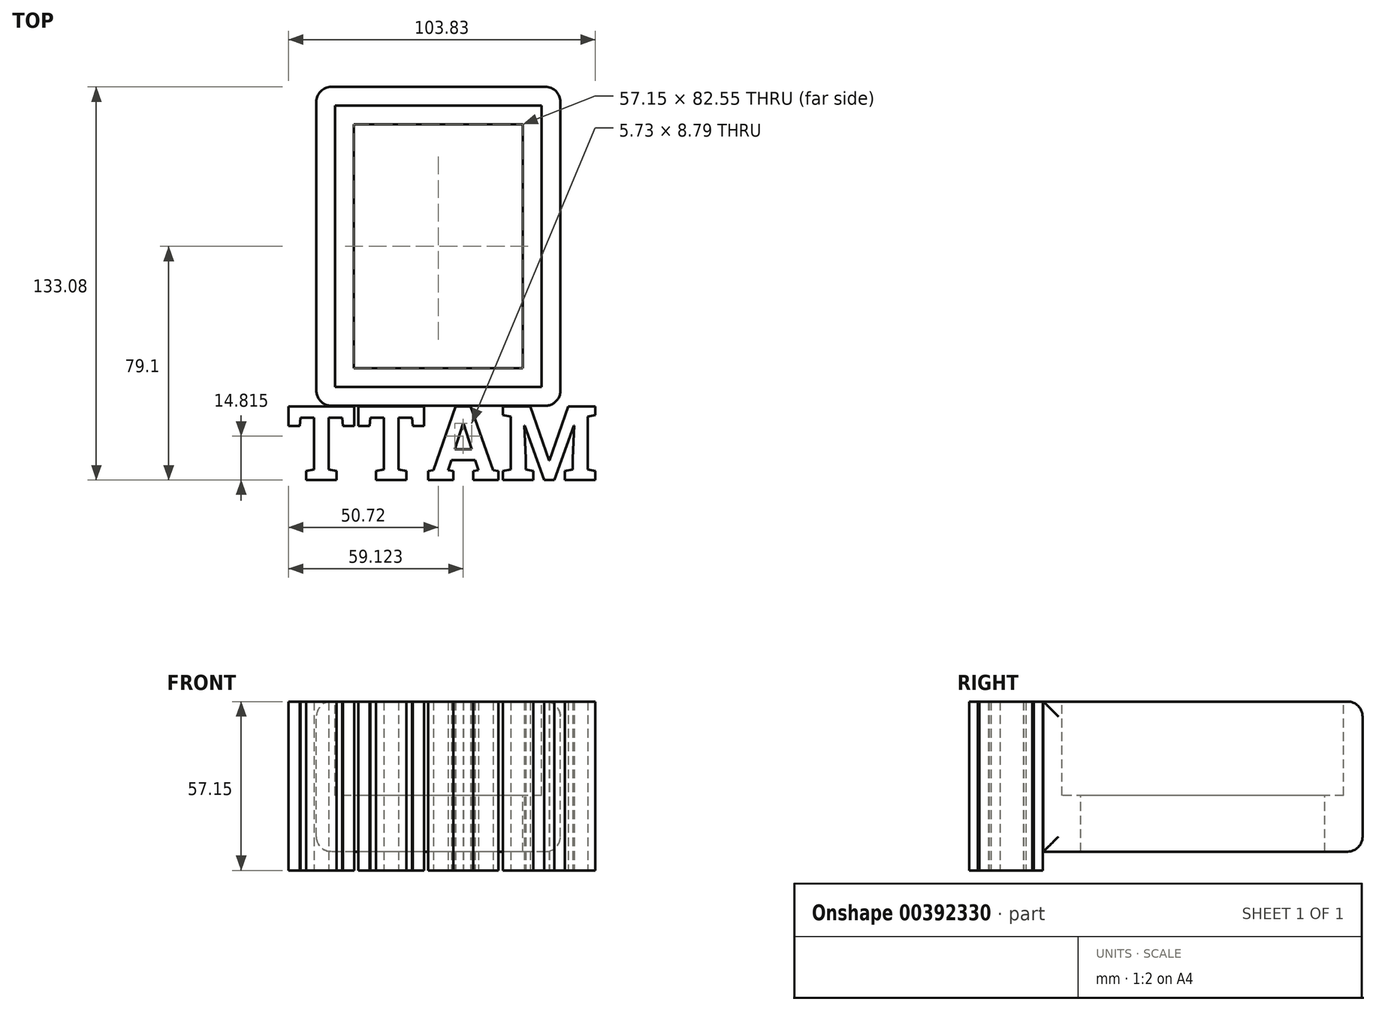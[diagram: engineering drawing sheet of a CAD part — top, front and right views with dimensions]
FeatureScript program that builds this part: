
annotation { "Feature Type Name" : "Feature", "Feature Type Description" : "" }
export const myFeature = defineFeature(function(context is Context, id is Id, definition is map)
    precondition{}
    {
        {
            var Q0;
            Q0=qCreatedBy(makeId("Top.planeOp"),FACE);
            var sketch = newSketch(context, id + "F0", { "sketchPlane" : qUnion([Q0])});
            skLineSegment(sketch, "E0.bottom", {"start": v(41.27, 53.98) * mm, "end": v(-41.28, 53.97) * mm});
            skLineSegment(sketch, "E0.top", {"start": v(41.28, -53.97) * mm, "end": v(-41.27, -53.98) * mm});
            skLineSegment(sketch, "E0.left", {"start": v(41.27, 53.98) * mm, "end": v(41.28, -53.97) * mm});
            skLineSegment(sketch, "E0.right", {"start": v(-41.28, 53.97) * mm, "end": v(-41.27, -53.98) * mm});
            skPoint(sketch, "E0.middle", {"position": v(0, 0) * mm});
            skSolve(sketch);
        }
        {
            var Q0;
            Q0=qCreatedBy(makeId("Top.planeOp"),FACE);
            var sketch = newSketch(context, id + "F1", { "sketchPlane" : qUnion([Q0])});
            skLineSegment(sketch, "E1.bottom", {"start": v(34.92, 47.63) * mm, "end": v(-34.93, 47.62) * mm});
            skLineSegment(sketch, "E1.top", {"start": v(34.93, -47.62) * mm, "end": v(-34.92, -47.63) * mm});
            skLineSegment(sketch, "E1.left", {"start": v(34.92, 47.63) * mm, "end": v(34.93, -47.62) * mm});
            skLineSegment(sketch, "E1.right", {"start": v(-34.93, 47.62) * mm, "end": v(-34.92, -47.63) * mm});
            skPoint(sketch, "E1.middle", {"position": v(0, 0) * mm});
            skSolve(sketch);
        }
        {
            var Q0;
            Q0=qCreatedBy(makeId("Top.planeOp"),FACE);
            var sketch = newSketch(context, id + "F2", { "sketchPlane" : qUnion([Q0])});
            skLineSegment(sketch, "E2.bottom", {"start": v(28.57, 41.28) * mm, "end": v(-28.58, 41.27) * mm});
            skLineSegment(sketch, "E2.top", {"start": v(28.58, -41.28) * mm, "end": v(-28.57, -41.28) * mm});
            skLineSegment(sketch, "E2.left", {"start": v(28.57, 41.28) * mm, "end": v(28.58, -41.28) * mm});
            skLineSegment(sketch, "E2.right", {"start": v(-28.58, 41.28) * mm, "end": v(-28.57, -41.28) * mm});
            skPoint(sketch, "E2.middle", {"position": v(0, 0) * mm});
            skSolve(sketch);
        }
        {
            var Q0;
            Q0=qCreatedBy(makeId("Top.planeOp"),FACE);
            var sketch = newSketch(context, id + "F3", { "sketchPlane" : qUnion([Q0])});
            skText(sketch, "E3", { "text": "MATT\n", "fontName": "RobotoSlab-Bold.ttf"});
            const initialGuessF3  = {"E3": [-0.05474, -0.0791, 1, 0, 0.02527]};
            skSetInitialGuess(sketch, initialGuessF3);
            skSolve(sketch);
        }
        {
            var Q0;
            Q0 = qSketchRegion(id + "F0", true);
            extrude(context, id + "F4", {"entities" : qUnion([Q0]), "oppositeDirection" : true, "depth" : 50.8 * mm});
        }
        {
            var Q0;
            Q0=makeQuery(id+"F1.imprint","IMPRINT",FACE,{"disambiguationData":[TD([[makeQuery(id+"F1.imprint","IMPRINT",EDGE,{"derivedFrom":sQuery(id+"F1.wireOp",EDGE,"E1.bottom")}),1.0]])]});
            extrude(context, id + "F5", {"entities" : qUnion([Q0]), "operationType" : NewBodyOperationType.REMOVE, "oppositeDirection" : true, "depth" : 31.75 * mm});
        }
        {
            var Q0;
            Q0=makeQuery(id+"F2.imprint","IMPRINT",FACE,{"disambiguationData":[TD([[makeQuery(id+"F2.imprint","IMPRINT",EDGE,{"derivedFrom":sQuery(id+"F2.wireOp",EDGE,"E2.bottom")}),1.0]])]});
            extrude(context, id + "F6", {"entities" : qUnion([Q0]), "operationType" : NewBodyOperationType.REMOVE, "oppositeDirection" : true, "depth" : 50.8 * mm});
        }
        {
            var Q0;
            Q0 = qSketchRegion(id + "F3", true);
            extrude(context, id + "F7", {"entities" : qUnion([Q0]), "operationType" : NewBodyOperationType.ADD, "oppositeDirection" : true, "depth" : 57.15 * mm});
        }
        {
            var Q0;
            Q0=makeQuery(id+"F4.opExtrude","SWEPT_FACE",FACE,{"disambiguationData":[OSD([sQuery(id+"F0.wireOp",EDGE,"E0.bottom")])]});
            var Q1;
            Q1=makeQuery(id+"F4.opExtrude","SWEPT_FACE",FACE,{"disambiguationData":[OSD([sQuery(id+"F0.wireOp",EDGE,"E0.left")])]});
            var Q2;
            Q2=makeQuery(id+"F4.opExtrude","SWEPT_FACE",FACE,{"disambiguationData":[OSD([sQuery(id+"F0.wireOp",EDGE,"E0.right")])]});
            fillet(context, id + "F8", {"entities" : qUnion([Q0, Q1, Q2]), "radius" : 5.08 * mm, "tangentPropagation" : true, "allowEdgeOverflow" : false});
        }
        {
            var Q0;
            Q0=makeQuery(id+"F7.opExtrude","SWEPT_BODY",BODY,{"disambiguationData":[OSD([sQuery(id+"F3.wireOp",EDGE,"E3.sketch_text.stroke-0"),sQuery(id+"F3.wireOp",EDGE,"E3.sketch_text.stroke-1"),sQuery(id+"F3.wireOp",EDGE,"E3.sketch_text.stroke-2"),sQuery(id+"F3.wireOp",EDGE,"E3.sketch_text.stroke-3"),sQuery(id+"F3.wireOp",EDGE,"E3.sketch_text.stroke-4"),sQuery(id+"F3.wireOp",EDGE,"E3.sketch_text.stroke-5"),sQuery(id+"F3.wireOp",EDGE,"E3.sketch_text.stroke-6"),sQuery(id+"F3.wireOp",EDGE,"E3.sketch_text.stroke-7"),sQuery(id+"F3.wireOp",EDGE,"E3.sketch_text.stroke-8"),sQuery(id+"F3.wireOp",EDGE,"E3.sketch_text.stroke-9"),sQuery(id+"F3.wireOp",EDGE,"E3.sketch_text.stroke-10"),sQuery(id+"F3.wireOp",EDGE,"E3.sketch_text.stroke-11"),sQuery(id+"F3.wireOp",EDGE,"E3.sketch_text.stroke-12"),sQuery(id+"F3.wireOp",EDGE,"E3.sketch_text.stroke-13"),sQuery(id+"F3.wireOp",EDGE,"E3.sketch_text.stroke-14"),sQuery(id+"F3.wireOp",EDGE,"E3.sketch_text.stroke-15"),sQuery(id+"F3.wireOp",EDGE,"E3.sketch_text.stroke-16"),sQuery(id+"F3.wireOp",EDGE,"E3.sketch_text.stroke-17"),sQuery(id+"F3.wireOp",EDGE,"E3.sketch_text.stroke-18"),sQuery(id+"F3.wireOp",EDGE,"E3.sketch_text.stroke-19"),sQuery(id+"F3.wireOp",EDGE,"E3.sketch_text.stroke-20"),sQuery(id+"F3.wireOp",EDGE,"E3.sketch_text.stroke-21"),sQuery(id+"F3.wireOp",EDGE,"E3.sketch_text.stroke-22"),sQuery(id+"F3.wireOp",EDGE,"E3.sketch_text.stroke-23"),sQuery(id+"F3.wireOp",EDGE,"E3.sketch_text.stroke-24"),sQuery(id+"F3.wireOp",EDGE,"E3.sketch_text.stroke-25"),sQuery(id+"F3.wireOp",EDGE,"E3.sketch_text.stroke-26"),sQuery(id+"F3.wireOp",EDGE,"E3.sketch_text.stroke-27"),sQuery(id+"F3.wireOp",EDGE,"E3.sketch_text.stroke-28"),sQuery(id+"F3.wireOp",EDGE,"E3.sketch_text.stroke-29"),sQuery(id+"F3.wireOp",EDGE,"E3.sketch_text.stroke-30")])]});
            var Q1;
            Q1=makeQuery(id+"F7.opExtrude","SWEPT_BODY",BODY,{"disambiguationData":[OSD([sQuery(id+"F3.wireOp",EDGE,"E3.sketch_text.stroke-31"),sQuery(id+"F3.wireOp",EDGE,"E3.sketch_text.stroke-32"),sQuery(id+"F3.wireOp",EDGE,"E3.sketch_text.stroke-33"),sQuery(id+"F3.wireOp",EDGE,"E3.sketch_text.stroke-34"),sQuery(id+"F3.wireOp",EDGE,"E3.sketch_text.stroke-35"),sQuery(id+"F3.wireOp",EDGE,"E3.sketch_text.stroke-36"),sQuery(id+"F3.wireOp",EDGE,"E3.sketch_text.stroke-37"),sQuery(id+"F3.wireOp",EDGE,"E3.sketch_text.stroke-38"),sQuery(id+"F3.wireOp",EDGE,"E3.sketch_text.stroke-39"),sQuery(id+"F3.wireOp",EDGE,"E3.sketch_text.stroke-40"),sQuery(id+"F3.wireOp",EDGE,"E3.sketch_text.stroke-41"),sQuery(id+"F3.wireOp",EDGE,"E3.sketch_text.stroke-42"),sQuery(id+"F3.wireOp",EDGE,"E3.sketch_text.stroke-43"),sQuery(id+"F3.wireOp",EDGE,"E3.sketch_text.stroke-44"),sQuery(id+"F3.wireOp",EDGE,"E3.sketch_text.stroke-45"),sQuery(id+"F3.wireOp",EDGE,"E3.sketch_text.stroke-46"),sQuery(id+"F3.wireOp",EDGE,"E3.sketch_text.stroke-47"),sQuery(id+"F3.wireOp",EDGE,"E3.sketch_text.stroke-48"),sQuery(id+"F3.wireOp",EDGE,"E3.sketch_text.stroke-49"),sQuery(id+"F3.wireOp",EDGE,"E3.sketch_text.stroke-50")])]});
            var Q2;
            Q2=makeQuery(id+"F7.opExtrude","SWEPT_BODY",BODY,{"disambiguationData":[OSD([sQuery(id+"F3.wireOp",EDGE,"E3.sketch_text.stroke-51"),sQuery(id+"F3.wireOp",EDGE,"E3.sketch_text.stroke-52"),sQuery(id+"F3.wireOp",EDGE,"E3.sketch_text.stroke-53"),sQuery(id+"F3.wireOp",EDGE,"E3.sketch_text.stroke-54"),sQuery(id+"F3.wireOp",EDGE,"E3.sketch_text.stroke-55"),sQuery(id+"F3.wireOp",EDGE,"E3.sketch_text.stroke-56"),sQuery(id+"F3.wireOp",EDGE,"E3.sketch_text.stroke-57"),sQuery(id+"F3.wireOp",EDGE,"E3.sketch_text.stroke-58"),sQuery(id+"F3.wireOp",EDGE,"E3.sketch_text.stroke-59"),sQuery(id+"F3.wireOp",EDGE,"E3.sketch_text.stroke-60"),sQuery(id+"F3.wireOp",EDGE,"E3.sketch_text.stroke-61"),sQuery(id+"F3.wireOp",EDGE,"E3.sketch_text.stroke-62"),sQuery(id+"F3.wireOp",EDGE,"E3.sketch_text.stroke-63"),sQuery(id+"F3.wireOp",EDGE,"E3.sketch_text.stroke-64"),sQuery(id+"F3.wireOp",EDGE,"E3.sketch_text.stroke-65"),sQuery(id+"F3.wireOp",EDGE,"E3.sketch_text.stroke-66")])]});
            var Q3;
            Q3=makeQuery(id+"F7.opExtrude","SWEPT_BODY",BODY,{"disambiguationData":[OSD([sQuery(id+"F3.wireOp",EDGE,"E3.sketch_text.stroke-67"),sQuery(id+"F3.wireOp",EDGE,"E3.sketch_text.stroke-68"),sQuery(id+"F3.wireOp",EDGE,"E3.sketch_text.stroke-69"),sQuery(id+"F3.wireOp",EDGE,"E3.sketch_text.stroke-70"),sQuery(id+"F3.wireOp",EDGE,"E3.sketch_text.stroke-71"),sQuery(id+"F3.wireOp",EDGE,"E3.sketch_text.stroke-72"),sQuery(id+"F3.wireOp",EDGE,"E3.sketch_text.stroke-73"),sQuery(id+"F3.wireOp",EDGE,"E3.sketch_text.stroke-74"),sQuery(id+"F3.wireOp",EDGE,"E3.sketch_text.stroke-75"),sQuery(id+"F3.wireOp",EDGE,"E3.sketch_text.stroke-76"),sQuery(id+"F3.wireOp",EDGE,"E3.sketch_text.stroke-77"),sQuery(id+"F3.wireOp",EDGE,"E3.sketch_text.stroke-78"),sQuery(id+"F3.wireOp",EDGE,"E3.sketch_text.stroke-79"),sQuery(id+"F3.wireOp",EDGE,"E3.sketch_text.stroke-80"),sQuery(id+"F3.wireOp",EDGE,"E3.sketch_text.stroke-81"),sQuery(id+"F3.wireOp",EDGE,"E3.sketch_text.stroke-82")])]});
            var Q4;
            Q4=makeQuery(id+"F7.opExtrude","CAP_EDGE",EDGE,{"disambiguationData":[OSD([sQuery(id+"F3.wireOp",EDGE,"E3.sketch_text.stroke-36")])],"isStart":true});
            transform(context, id + "F9", {"entities" : qUnion([Q0, Q1, Q2, Q3]), "transformType" : TransformType.ROTATION, "transformAxis" : qUnion([Q4]), "angle" : 180 * degree, "makeCopy" : false});
        }
        {
            var Q0;
            Q0=makeQuery(id+"F7.opExtrude","SWEPT_BODY",BODY,{"disambiguationData":[OSD([sQuery(id+"F3.wireOp",EDGE,"E3.sketch_text.stroke-67"),sQuery(id+"F3.wireOp",EDGE,"E3.sketch_text.stroke-68"),sQuery(id+"F3.wireOp",EDGE,"E3.sketch_text.stroke-69"),sQuery(id+"F3.wireOp",EDGE,"E3.sketch_text.stroke-70"),sQuery(id+"F3.wireOp",EDGE,"E3.sketch_text.stroke-71"),sQuery(id+"F3.wireOp",EDGE,"E3.sketch_text.stroke-72"),sQuery(id+"F3.wireOp",EDGE,"E3.sketch_text.stroke-73"),sQuery(id+"F3.wireOp",EDGE,"E3.sketch_text.stroke-74"),sQuery(id+"F3.wireOp",EDGE,"E3.sketch_text.stroke-75"),sQuery(id+"F3.wireOp",EDGE,"E3.sketch_text.stroke-76"),sQuery(id+"F3.wireOp",EDGE,"E3.sketch_text.stroke-77"),sQuery(id+"F3.wireOp",EDGE,"E3.sketch_text.stroke-78"),sQuery(id+"F3.wireOp",EDGE,"E3.sketch_text.stroke-79"),sQuery(id+"F3.wireOp",EDGE,"E3.sketch_text.stroke-80"),sQuery(id+"F3.wireOp",EDGE,"E3.sketch_text.stroke-81"),sQuery(id+"F3.wireOp",EDGE,"E3.sketch_text.stroke-82")])]});
            var Q1;
            Q1=makeQuery(id+"F7.opExtrude","SWEPT_BODY",BODY,{"disambiguationData":[OSD([sQuery(id+"F3.wireOp",EDGE,"E3.sketch_text.stroke-51"),sQuery(id+"F3.wireOp",EDGE,"E3.sketch_text.stroke-52"),sQuery(id+"F3.wireOp",EDGE,"E3.sketch_text.stroke-53"),sQuery(id+"F3.wireOp",EDGE,"E3.sketch_text.stroke-54"),sQuery(id+"F3.wireOp",EDGE,"E3.sketch_text.stroke-55"),sQuery(id+"F3.wireOp",EDGE,"E3.sketch_text.stroke-56"),sQuery(id+"F3.wireOp",EDGE,"E3.sketch_text.stroke-57"),sQuery(id+"F3.wireOp",EDGE,"E3.sketch_text.stroke-58"),sQuery(id+"F3.wireOp",EDGE,"E3.sketch_text.stroke-59"),sQuery(id+"F3.wireOp",EDGE,"E3.sketch_text.stroke-60"),sQuery(id+"F3.wireOp",EDGE,"E3.sketch_text.stroke-61"),sQuery(id+"F3.wireOp",EDGE,"E3.sketch_text.stroke-62"),sQuery(id+"F3.wireOp",EDGE,"E3.sketch_text.stroke-63"),sQuery(id+"F3.wireOp",EDGE,"E3.sketch_text.stroke-64"),sQuery(id+"F3.wireOp",EDGE,"E3.sketch_text.stroke-65"),sQuery(id+"F3.wireOp",EDGE,"E3.sketch_text.stroke-66")])]});
            var Q2;
            Q2=makeQuery(id+"F7.opExtrude","SWEPT_BODY",BODY,{"disambiguationData":[OSD([sQuery(id+"F3.wireOp",EDGE,"E3.sketch_text.stroke-31"),sQuery(id+"F3.wireOp",EDGE,"E3.sketch_text.stroke-32"),sQuery(id+"F3.wireOp",EDGE,"E3.sketch_text.stroke-33"),sQuery(id+"F3.wireOp",EDGE,"E3.sketch_text.stroke-34"),sQuery(id+"F3.wireOp",EDGE,"E3.sketch_text.stroke-35"),sQuery(id+"F3.wireOp",EDGE,"E3.sketch_text.stroke-36"),sQuery(id+"F3.wireOp",EDGE,"E3.sketch_text.stroke-37"),sQuery(id+"F3.wireOp",EDGE,"E3.sketch_text.stroke-38"),sQuery(id+"F3.wireOp",EDGE,"E3.sketch_text.stroke-39"),sQuery(id+"F3.wireOp",EDGE,"E3.sketch_text.stroke-40"),sQuery(id+"F3.wireOp",EDGE,"E3.sketch_text.stroke-41"),sQuery(id+"F3.wireOp",EDGE,"E3.sketch_text.stroke-42"),sQuery(id+"F3.wireOp",EDGE,"E3.sketch_text.stroke-43"),sQuery(id+"F3.wireOp",EDGE,"E3.sketch_text.stroke-44"),sQuery(id+"F3.wireOp",EDGE,"E3.sketch_text.stroke-45"),sQuery(id+"F3.wireOp",EDGE,"E3.sketch_text.stroke-46"),sQuery(id+"F3.wireOp",EDGE,"E3.sketch_text.stroke-47"),sQuery(id+"F3.wireOp",EDGE,"E3.sketch_text.stroke-48"),sQuery(id+"F3.wireOp",EDGE,"E3.sketch_text.stroke-49"),sQuery(id+"F3.wireOp",EDGE,"E3.sketch_text.stroke-50")])]});
            var Q3;
            Q3=makeQuery(id+"F7.opExtrude","SWEPT_BODY",BODY,{"disambiguationData":[OSD([sQuery(id+"F3.wireOp",EDGE,"E3.sketch_text.stroke-0"),sQuery(id+"F3.wireOp",EDGE,"E3.sketch_text.stroke-1"),sQuery(id+"F3.wireOp",EDGE,"E3.sketch_text.stroke-2"),sQuery(id+"F3.wireOp",EDGE,"E3.sketch_text.stroke-3"),sQuery(id+"F3.wireOp",EDGE,"E3.sketch_text.stroke-4"),sQuery(id+"F3.wireOp",EDGE,"E3.sketch_text.stroke-5"),sQuery(id+"F3.wireOp",EDGE,"E3.sketch_text.stroke-6"),sQuery(id+"F3.wireOp",EDGE,"E3.sketch_text.stroke-7"),sQuery(id+"F3.wireOp",EDGE,"E3.sketch_text.stroke-8"),sQuery(id+"F3.wireOp",EDGE,"E3.sketch_text.stroke-9"),sQuery(id+"F3.wireOp",EDGE,"E3.sketch_text.stroke-10"),sQuery(id+"F3.wireOp",EDGE,"E3.sketch_text.stroke-11"),sQuery(id+"F3.wireOp",EDGE,"E3.sketch_text.stroke-12"),sQuery(id+"F3.wireOp",EDGE,"E3.sketch_text.stroke-13"),sQuery(id+"F3.wireOp",EDGE,"E3.sketch_text.stroke-14"),sQuery(id+"F3.wireOp",EDGE,"E3.sketch_text.stroke-15"),sQuery(id+"F3.wireOp",EDGE,"E3.sketch_text.stroke-16"),sQuery(id+"F3.wireOp",EDGE,"E3.sketch_text.stroke-17"),sQuery(id+"F3.wireOp",EDGE,"E3.sketch_text.stroke-18"),sQuery(id+"F3.wireOp",EDGE,"E3.sketch_text.stroke-19"),sQuery(id+"F3.wireOp",EDGE,"E3.sketch_text.stroke-20"),sQuery(id+"F3.wireOp",EDGE,"E3.sketch_text.stroke-21"),sQuery(id+"F3.wireOp",EDGE,"E3.sketch_text.stroke-22"),sQuery(id+"F3.wireOp",EDGE,"E3.sketch_text.stroke-23"),sQuery(id+"F3.wireOp",EDGE,"E3.sketch_text.stroke-24"),sQuery(id+"F3.wireOp",EDGE,"E3.sketch_text.stroke-25"),sQuery(id+"F3.wireOp",EDGE,"E3.sketch_text.stroke-26"),sQuery(id+"F3.wireOp",EDGE,"E3.sketch_text.stroke-27"),sQuery(id+"F3.wireOp",EDGE,"E3.sketch_text.stroke-28"),sQuery(id+"F3.wireOp",EDGE,"E3.sketch_text.stroke-29"),sQuery(id+"F3.wireOp",EDGE,"E3.sketch_text.stroke-30")])]});
            var Q4;
            {var subQ0=sQuery(id+"F0.wireOp",EDGE,"E0.top");Q4=makeQuery(id+"F8.opFillet","BLEND_EDGE",EDGE,{"blendedFrom":[makeQuery(id+"F4.opExtrude","SWEPT_EDGE",EDGE,{"disambiguationData":[OSD([subQ0,sQuery(id+"F0.wireOp",EDGE,"E0.left")])]}),makeQuery(id+"F4.opExtrude","SWEPT_FACE",FACE,{"disambiguationData":[OSD([subQ0])]})],"blendedInto":[makeQuery(id+"F4.opExtrude","SWEPT_FACE",FACE,{"disambiguationData":[OSD([subQ0])]})]});}
            transform(context, id + "F10", {"entities" : qUnion([Q0, Q1, Q2, Q3]), "transformType" : TransformType.TRANSLATION_DISTANCE, "transformDirection" : qUnion([Q4]), "distance" : 57.15 * mm, "oppositeDirection" : true, "makeCopy" : false});
        }
        {
            var Q0;
            Q0=makeQuery(id+"F7.opExtrude","SWEPT_BODY",BODY,{"disambiguationData":[OSD([sQuery(id+"F3.wireOp",EDGE,"E3.sketch_text.stroke-67"),sQuery(id+"F3.wireOp",EDGE,"E3.sketch_text.stroke-68"),sQuery(id+"F3.wireOp",EDGE,"E3.sketch_text.stroke-69"),sQuery(id+"F3.wireOp",EDGE,"E3.sketch_text.stroke-70"),sQuery(id+"F3.wireOp",EDGE,"E3.sketch_text.stroke-71"),sQuery(id+"F3.wireOp",EDGE,"E3.sketch_text.stroke-72"),sQuery(id+"F3.wireOp",EDGE,"E3.sketch_text.stroke-73"),sQuery(id+"F3.wireOp",EDGE,"E3.sketch_text.stroke-74"),sQuery(id+"F3.wireOp",EDGE,"E3.sketch_text.stroke-75"),sQuery(id+"F3.wireOp",EDGE,"E3.sketch_text.stroke-76"),sQuery(id+"F3.wireOp",EDGE,"E3.sketch_text.stroke-77"),sQuery(id+"F3.wireOp",EDGE,"E3.sketch_text.stroke-78"),sQuery(id+"F3.wireOp",EDGE,"E3.sketch_text.stroke-79"),sQuery(id+"F3.wireOp",EDGE,"E3.sketch_text.stroke-80"),sQuery(id+"F3.wireOp",EDGE,"E3.sketch_text.stroke-81"),sQuery(id+"F3.wireOp",EDGE,"E3.sketch_text.stroke-82")])]});
            var Q1;
            Q1=makeQuery(id+"F7.opExtrude","SWEPT_BODY",BODY,{"disambiguationData":[OSD([sQuery(id+"F3.wireOp",EDGE,"E3.sketch_text.stroke-51"),sQuery(id+"F3.wireOp",EDGE,"E3.sketch_text.stroke-52"),sQuery(id+"F3.wireOp",EDGE,"E3.sketch_text.stroke-53"),sQuery(id+"F3.wireOp",EDGE,"E3.sketch_text.stroke-54"),sQuery(id+"F3.wireOp",EDGE,"E3.sketch_text.stroke-55"),sQuery(id+"F3.wireOp",EDGE,"E3.sketch_text.stroke-56"),sQuery(id+"F3.wireOp",EDGE,"E3.sketch_text.stroke-57"),sQuery(id+"F3.wireOp",EDGE,"E3.sketch_text.stroke-58"),sQuery(id+"F3.wireOp",EDGE,"E3.sketch_text.stroke-59"),sQuery(id+"F3.wireOp",EDGE,"E3.sketch_text.stroke-60"),sQuery(id+"F3.wireOp",EDGE,"E3.sketch_text.stroke-61"),sQuery(id+"F3.wireOp",EDGE,"E3.sketch_text.stroke-62"),sQuery(id+"F3.wireOp",EDGE,"E3.sketch_text.stroke-63"),sQuery(id+"F3.wireOp",EDGE,"E3.sketch_text.stroke-64"),sQuery(id+"F3.wireOp",EDGE,"E3.sketch_text.stroke-65"),sQuery(id+"F3.wireOp",EDGE,"E3.sketch_text.stroke-66")])]});
            var Q2;
            Q2=makeQuery(id+"F7.opExtrude","SWEPT_BODY",BODY,{"disambiguationData":[OSD([sQuery(id+"F3.wireOp",EDGE,"E3.sketch_text.stroke-31"),sQuery(id+"F3.wireOp",EDGE,"E3.sketch_text.stroke-32"),sQuery(id+"F3.wireOp",EDGE,"E3.sketch_text.stroke-33"),sQuery(id+"F3.wireOp",EDGE,"E3.sketch_text.stroke-34"),sQuery(id+"F3.wireOp",EDGE,"E3.sketch_text.stroke-35"),sQuery(id+"F3.wireOp",EDGE,"E3.sketch_text.stroke-36"),sQuery(id+"F3.wireOp",EDGE,"E3.sketch_text.stroke-37"),sQuery(id+"F3.wireOp",EDGE,"E3.sketch_text.stroke-38"),sQuery(id+"F3.wireOp",EDGE,"E3.sketch_text.stroke-39"),sQuery(id+"F3.wireOp",EDGE,"E3.sketch_text.stroke-40"),sQuery(id+"F3.wireOp",EDGE,"E3.sketch_text.stroke-41"),sQuery(id+"F3.wireOp",EDGE,"E3.sketch_text.stroke-42"),sQuery(id+"F3.wireOp",EDGE,"E3.sketch_text.stroke-43"),sQuery(id+"F3.wireOp",EDGE,"E3.sketch_text.stroke-44"),sQuery(id+"F3.wireOp",EDGE,"E3.sketch_text.stroke-45"),sQuery(id+"F3.wireOp",EDGE,"E3.sketch_text.stroke-46"),sQuery(id+"F3.wireOp",EDGE,"E3.sketch_text.stroke-47"),sQuery(id+"F3.wireOp",EDGE,"E3.sketch_text.stroke-48"),sQuery(id+"F3.wireOp",EDGE,"E3.sketch_text.stroke-49"),sQuery(id+"F3.wireOp",EDGE,"E3.sketch_text.stroke-50")])]});
            var Q3;
            Q3=makeQuery(id+"F7.opExtrude","SWEPT_BODY",BODY,{"disambiguationData":[OSD([sQuery(id+"F3.wireOp",EDGE,"E3.sketch_text.stroke-0"),sQuery(id+"F3.wireOp",EDGE,"E3.sketch_text.stroke-1"),sQuery(id+"F3.wireOp",EDGE,"E3.sketch_text.stroke-2"),sQuery(id+"F3.wireOp",EDGE,"E3.sketch_text.stroke-3"),sQuery(id+"F3.wireOp",EDGE,"E3.sketch_text.stroke-4"),sQuery(id+"F3.wireOp",EDGE,"E3.sketch_text.stroke-5"),sQuery(id+"F3.wireOp",EDGE,"E3.sketch_text.stroke-6"),sQuery(id+"F3.wireOp",EDGE,"E3.sketch_text.stroke-7"),sQuery(id+"F3.wireOp",EDGE,"E3.sketch_text.stroke-8"),sQuery(id+"F3.wireOp",EDGE,"E3.sketch_text.stroke-9"),sQuery(id+"F3.wireOp",EDGE,"E3.sketch_text.stroke-10"),sQuery(id+"F3.wireOp",EDGE,"E3.sketch_text.stroke-11"),sQuery(id+"F3.wireOp",EDGE,"E3.sketch_text.stroke-12"),sQuery(id+"F3.wireOp",EDGE,"E3.sketch_text.stroke-13"),sQuery(id+"F3.wireOp",EDGE,"E3.sketch_text.stroke-14"),sQuery(id+"F3.wireOp",EDGE,"E3.sketch_text.stroke-15"),sQuery(id+"F3.wireOp",EDGE,"E3.sketch_text.stroke-16"),sQuery(id+"F3.wireOp",EDGE,"E3.sketch_text.stroke-17"),sQuery(id+"F3.wireOp",EDGE,"E3.sketch_text.stroke-18"),sQuery(id+"F3.wireOp",EDGE,"E3.sketch_text.stroke-19"),sQuery(id+"F3.wireOp",EDGE,"E3.sketch_text.stroke-20"),sQuery(id+"F3.wireOp",EDGE,"E3.sketch_text.stroke-21"),sQuery(id+"F3.wireOp",EDGE,"E3.sketch_text.stroke-22"),sQuery(id+"F3.wireOp",EDGE,"E3.sketch_text.stroke-23"),sQuery(id+"F3.wireOp",EDGE,"E3.sketch_text.stroke-24"),sQuery(id+"F3.wireOp",EDGE,"E3.sketch_text.stroke-25"),sQuery(id+"F3.wireOp",EDGE,"E3.sketch_text.stroke-26"),sQuery(id+"F3.wireOp",EDGE,"E3.sketch_text.stroke-27"),sQuery(id+"F3.wireOp",EDGE,"E3.sketch_text.stroke-28"),sQuery(id+"F3.wireOp",EDGE,"E3.sketch_text.stroke-29"),sQuery(id+"F3.wireOp",EDGE,"E3.sketch_text.stroke-30")])]});
            transform(context, id + "F11", {"entities" : qUnion([Q0, Q1, Q2, Q3]), "transformType" : TransformType.TRANSLATION_3D, "dx" : -6.35 * mm, "dy" : 0 * mm, "dz" : 0 * mm, "makeCopy" : false});
        }
    });
